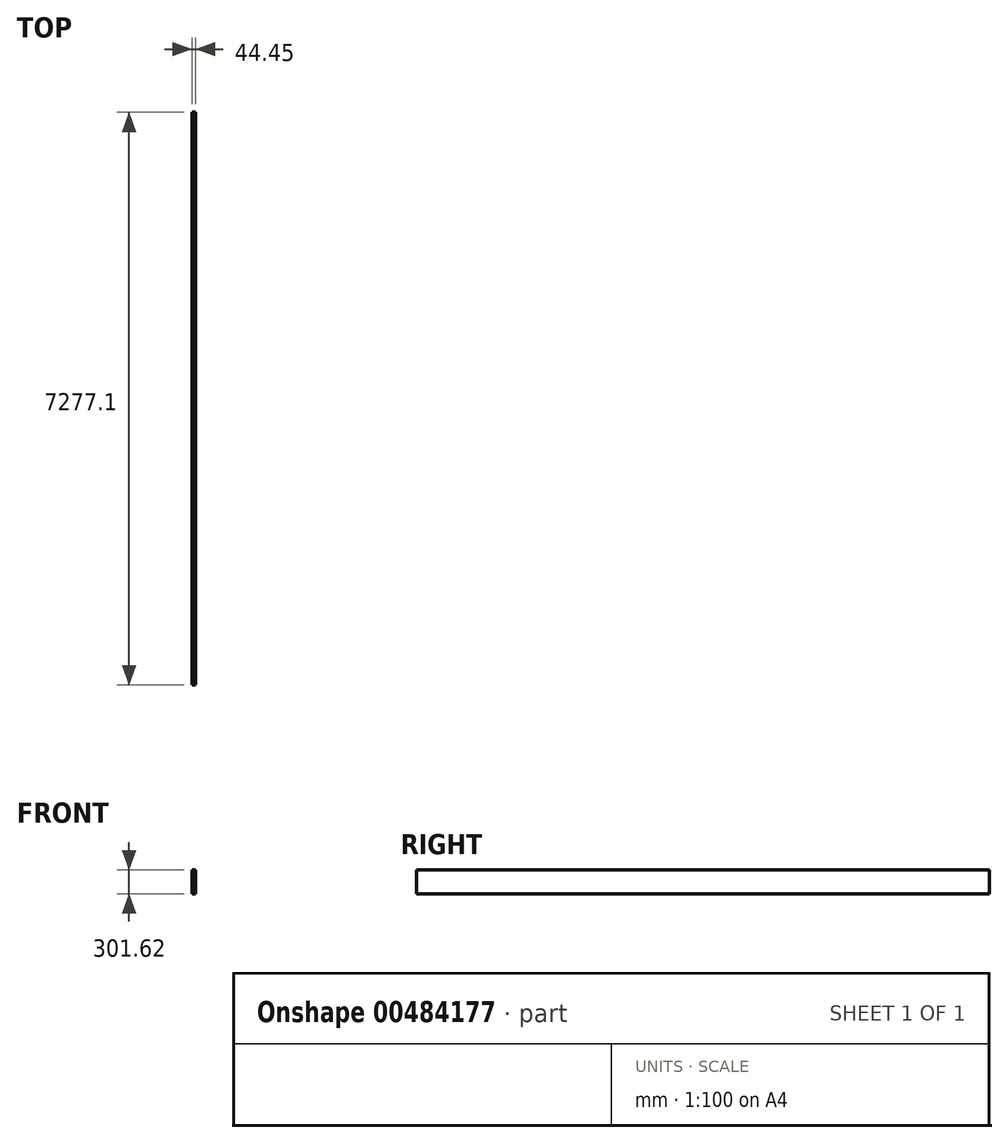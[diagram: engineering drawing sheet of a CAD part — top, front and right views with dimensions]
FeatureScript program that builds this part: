
annotation { "Feature Type Name" : "Feature", "Feature Type Description" : "" }
export const myFeature = defineFeature(function(context is Context, id is Id, definition is map)
    precondition{}
    {
        {
            var Q0;
            Q0=qCreatedBy(makeId("Front.planeOp"),FACE);
            var sketch = newSketch(context, id + "F0", { "sketchPlane" : qUnion([Q0])});
            skLineSegment(sketch, "E0.bottom", {"start": v(0, 0) * mm, "end": v(44.45, 0) * mm});
            skLineSegment(sketch, "E0.top", {"start": v(0, 301.63) * mm, "end": v(44.45, 301.63) * mm});
            skLineSegment(sketch, "E0.left", {"start": v(0, 0) * mm, "end": v(0, 301.63) * mm});
            skLineSegment(sketch, "E0.right", {"start": v(44.45, 0) * mm, "end": v(44.45, 301.63) * mm});
            skSolve(sketch);
        }
        {
            var Q0;
            Q0 = qSketchRegion(id + "F0", true);
            extrude(context, id + "F1", {"entities" : qUnion([Q0]), "depth" : 7277.1 * mm});
        }
    });
